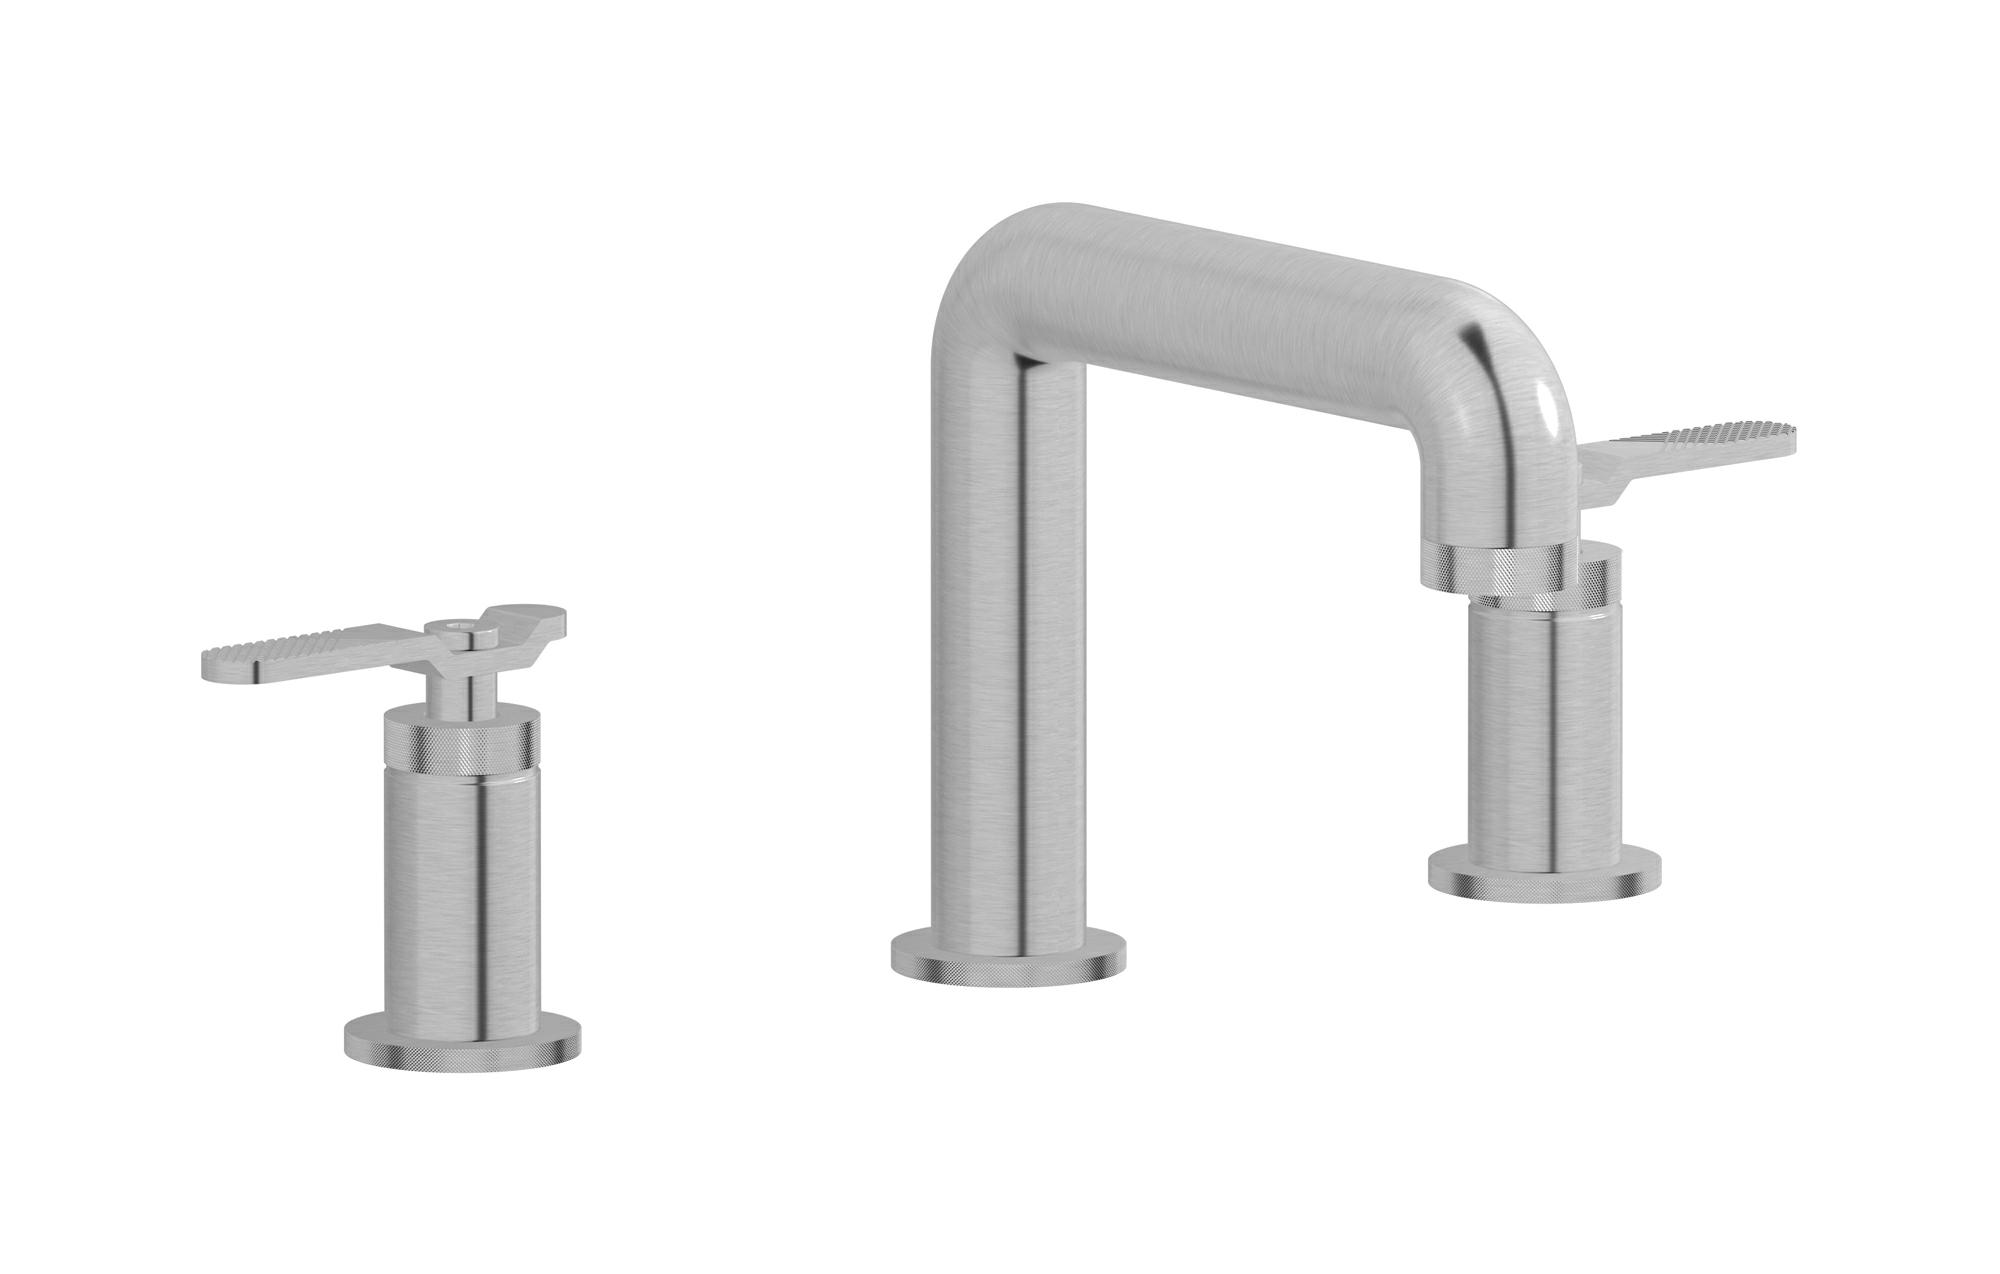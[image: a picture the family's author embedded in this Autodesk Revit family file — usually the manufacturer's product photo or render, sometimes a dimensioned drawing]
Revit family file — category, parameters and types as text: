
# Revit family: B2392
name_source: partatom
category: Apparecchi idraulici
units: mm (PartAtom-declared; Revit-internal decimal feet)

## family parameters
Basato su piano di lavoro = No
Condiviso = No
Mantieni orientamento annotazione = No
Numero OmniClass = 23.45.55.17
Punto di calcolo locali = No
Quota connettore circolare = Usa diametro
Sempre verticale = Sì
Taglio con vuoti quando caricato = No
Tipo di parte = Normale
Titolo OmniClass = Mixing Faucets

## types (13) — shared parameters
Cold water inlet = 10 mm  [stored 0.0328084 ft]
Commenti sul tipo = Three holes washbasin set with low spout
Connessione CW = No
Connessione HW = No
Connessione di scarico = No
Connessione di ventilazione = No
Descrizione = Three holes washbasin set with low spout
Hot water inlet = 10 mm  [stored 0.0328084 ft]
Produttore = IB Rubinetterie S.p.A.
URL = https://www.weareib.it
zero-valued in all types: Prospetto di default

## per-type parameters (varying)
| type | Finishes surface | Immagine tipo | Modello |
| Chrome | IB_Chrome | B2392CC.jpg | B2392CC |
| Black Chrome | IB_Black chrome | B2392CF.jpg | B2392CF |
| Brushed Black Chrome | IB_Brushed black chrome | B2392CS.jpg | B2392CS |
| Pale Gold | IB_Pale gold | B2392II.jpg | B2392II |
| Brushed Pale Gold | IB_brushed pale gold | B2392IS.jpg | B2392IS |
| Matt Black | IB_matt black | B2392NP.jpg | B2392NP |
| Natural Brass | IB_Brass | B2392ON.jpg | B2392ON |
| Gold | IB_gold | B2392OO.jpg | B2392OO |
| Brushed Gold | IB_brushed gold | B2392OS.jpg | B2392OS |
| Rose Gold | IB_Rose gold | B2392RS.jpg | B2392RS |
| Brushed Rose Gold | IB_Brushed rose gold | B2392SR.jpg | B2392SR |
| Brushed Nickel | IB_Brushed nickel | B2392SS.jpg | B2392SS |
| Modern Bronze | IB_Modern bronze | B2392MB.jpg | B2392MB |

note: [stored X ft] marks values corroborated as IEEE doubles in the binary element streams (Revit-internal decimal feet)
